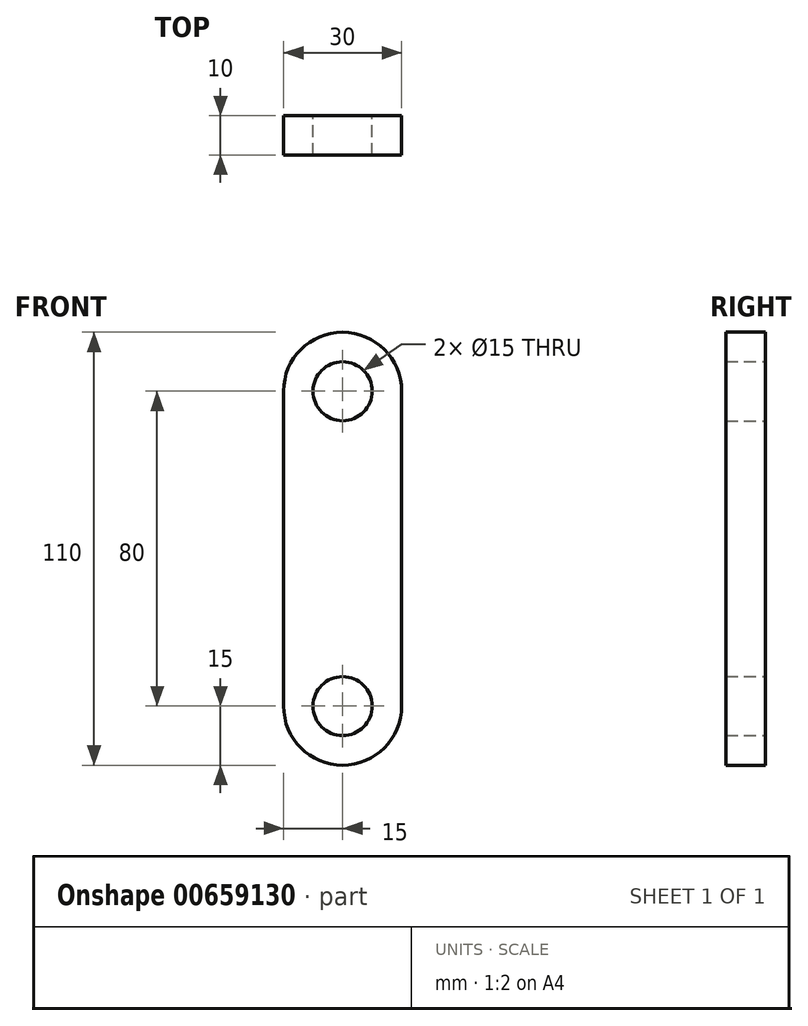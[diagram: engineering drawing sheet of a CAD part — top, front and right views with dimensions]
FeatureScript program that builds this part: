
annotation { "Feature Type Name" : "Feature", "Feature Type Description" : "" }
export const myFeature = defineFeature(function(context is Context, id is Id, definition is map)
    precondition{}
    {
        {
            var Q0;
            Q0=qCreatedBy(makeId("Front.planeOp"),FACE);
            var sketch = newSketch(context, id + "F0", { "sketchPlane" : qUnion([Q0])});
            skLineSegment(sketch, "E0", {"start": v(0, 55) * mm, "end": v(0, 0) * mm, "construction": true});
            skLineSegment(sketch, "E1", {"start": v(-15, 0) * mm, "end": v(15, 0) * mm, "construction": true});
            skCircle(sketch, "E2", {"center": v(0, 40) * mm, "radius": 7.5 * mm});
            skArc(sketch, "E3", {"start": v(15, 40) * mm, "mid": v(0, 55) * mm, "end": v(-15, 40) * mm});
            skLineSegment(sketch, "E4", {"start": v(-15, 40) * mm, "end": v(-15, 0) * mm});
            skLineSegment(sketch, "E5", {"start": v(15, 40) * mm, "end": v(15, 0) * mm});
            skArc(sketch, "E6.MirrorCS", {"start": v(15, -40) * mm, "mid": v(0, -55) * mm, "end": v(-15, -40) * mm});
            skCircle(sketch, "E7.MirrorC", {"center": v(0, -40) * mm, "radius": 7.5 * mm});
            skLineSegment(sketch, "E8.MirrorCS", {"start": v(15, -40) * mm, "end": v(15, 0) * mm});
            skLineSegment(sketch, "E9.MirrorCS", {"start": v(-15, -40) * mm, "end": v(-15, 0) * mm});
            skSolve(sketch);
        }
        {
            var Q0;
            Q0=qSketchRegion(id+"F0",true);
            extrude(context, id + "F1", {"entities" : qUnion([Q0]), "depth" : 10 * mm, "offsetDistance" : 25 * mm});
        }
    });
